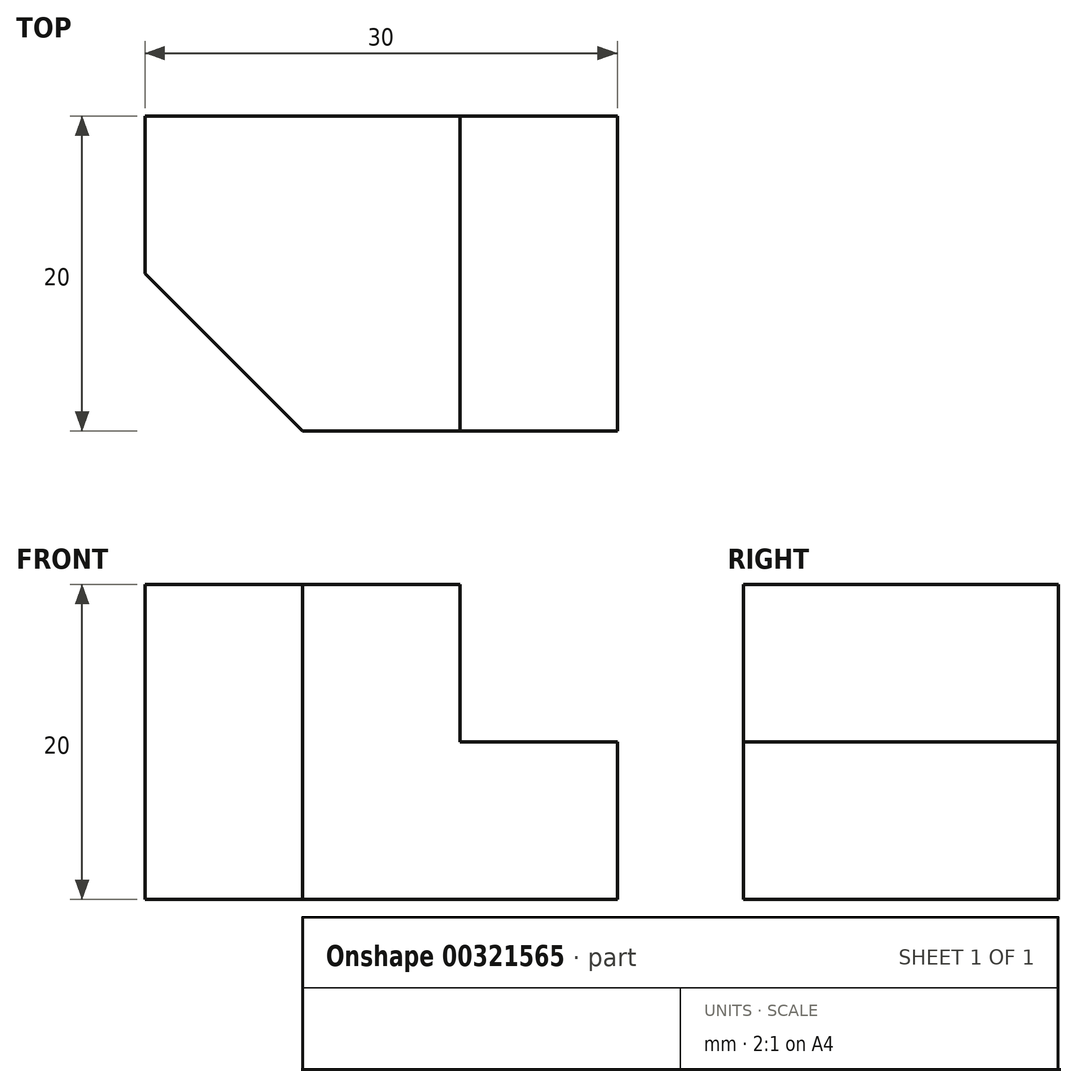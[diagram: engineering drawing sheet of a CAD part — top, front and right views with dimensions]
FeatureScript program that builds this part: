
annotation { "Feature Type Name" : "Feature", "Feature Type Description" : "" }
export const myFeature = defineFeature(function(context is Context, id is Id, definition is map)
    precondition{}
    {
        {
            var Q0;
            Q0=qCreatedBy(makeId("Top.planeOp"),FACE);
            var sketch = newSketch(context, id + "F0", { "sketchPlane" : qUnion([Q0])});
            skLineSegment(sketch, "E0", {"start": v(0, 10) * mm, "end": v(0, 20) * mm});
            skLineSegment(sketch, "E1", {"start": v(0, 20) * mm, "end": v(20, 20) * mm});
            skLineSegment(sketch, "E2", {"start": v(20, 20) * mm, "end": v(20, 0) * mm});
            skLineSegment(sketch, "E3", {"start": v(20, 0) * mm, "end": v(10, 0) * mm});
            skLineSegment(sketch, "E4", {"start": v(10, 0) * mm, "end": v(0, 10) * mm});
            skSolve(sketch);
        }
        {
            var Q0;
            Q0=makeQuery(id+"F0.imprint","IMPRINT",FACE,{"disambiguationData":[TD([[makeQuery(id+"F0.imprint","IMPRINT",EDGE,{"derivedFrom":sQuery(id+"F0.wireOp",EDGE,"E0")}),-1.0]])]});
            extrude(context, id + "F1", {"entities" : qUnion([Q0]), "depth" : 20 * mm});
        }
        {
            var Q0;
            Q0=qCreatedBy(makeId("Top.planeOp"),FACE);
            var sketch = newSketch(context, id + "F2", { "sketchPlane" : qUnion([Q0])});
            skLineSegment(sketch, "E5.bottom", {"start": v(20, 20) * mm, "end": v(30, 20) * mm});
            skLineSegment(sketch, "E5.top", {"start": v(20, 0) * mm, "end": v(30, 0) * mm});
            skLineSegment(sketch, "E5.left", {"start": v(20, 20) * mm, "end": v(20, 0) * mm});
            skLineSegment(sketch, "E5.right", {"start": v(30, 20) * mm, "end": v(30, 0) * mm});
            skSolve(sketch);
        }
        {
            var Q0;
            Q0=makeQuery(id+"F2.imprint","IMPRINT",FACE,{"disambiguationData":[TD([[makeQuery(id+"F2.imprint","IMPRINT",EDGE,{"derivedFrom":sQuery(id+"F2.wireOp",EDGE,"E5.bottom")}),-1.0]])]});
            extrude(context, id + "F3", {"entities" : qUnion([Q0]), "operationType" : NewBodyOperationType.ADD, "depth" : 10 * mm});
        }
    });
